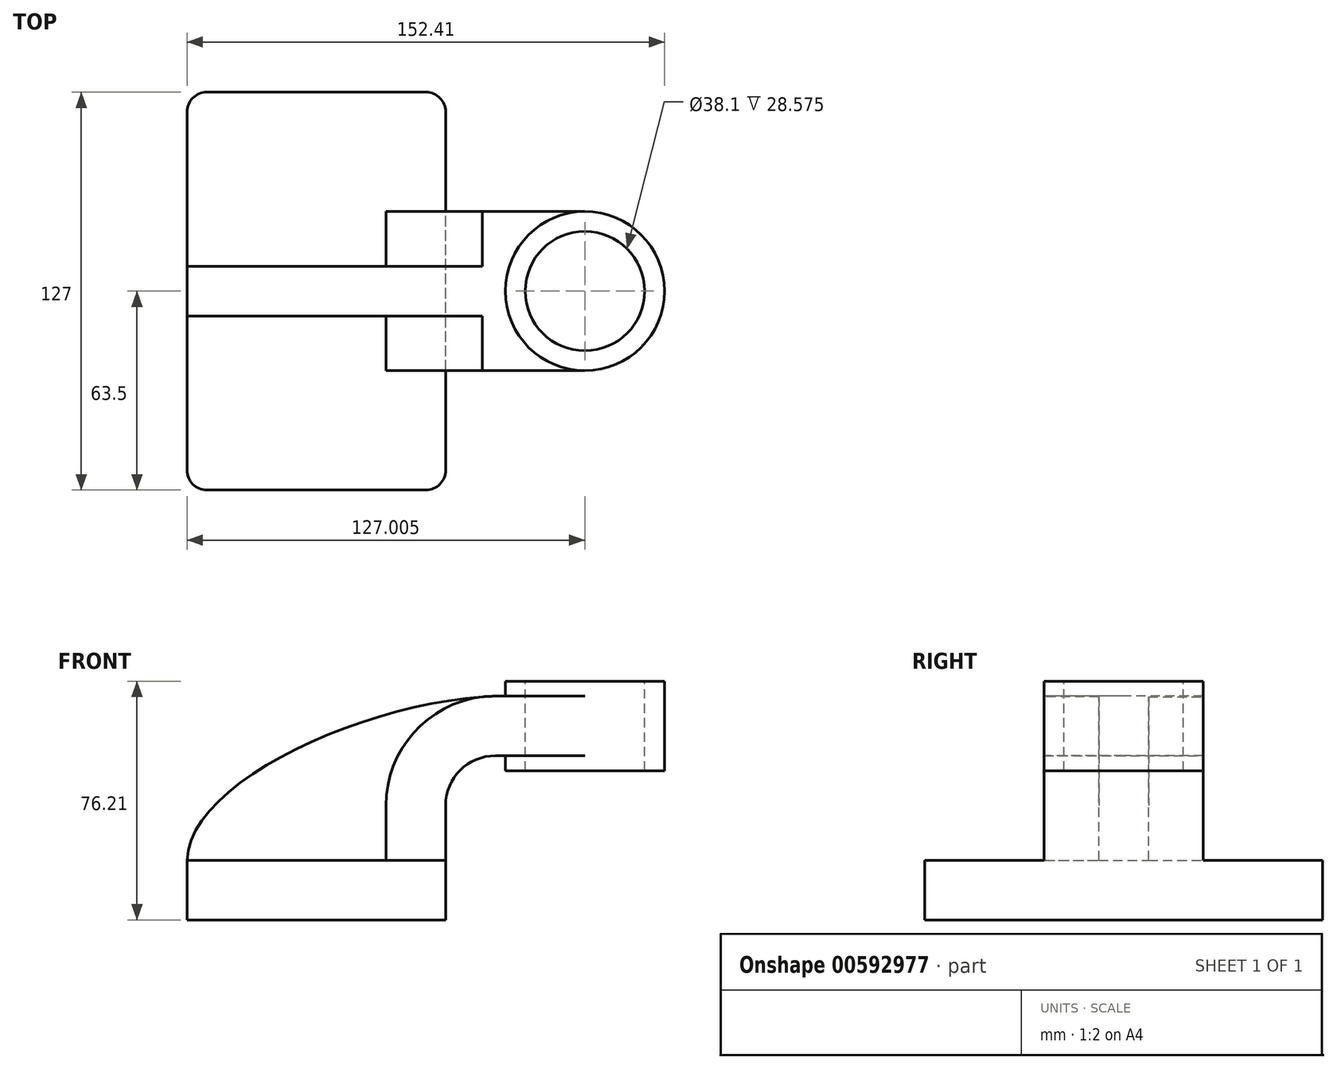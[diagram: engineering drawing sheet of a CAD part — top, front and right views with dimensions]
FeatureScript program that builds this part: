
annotation { "Feature Type Name" : "Feature", "Feature Type Description" : "" }
export const myFeature = defineFeature(function(context is Context, id is Id, definition is map)
    precondition{}
    {
        {
            var Q0;
            Q0=qCreatedBy(makeId("Front.planeOp"),FACE);
            var sketch = newSketch(context, id + "F0", { "sketchPlane" : qUnion([Q0])});
            skLineSegment(sketch, "E0.bottom", {"start": v(-41.27, 9.53) * mm, "end": v(41.28, 9.53) * mm});
            skLineSegment(sketch, "E0.top", {"start": v(-41.28, -9.52) * mm, "end": v(41.27, -9.52) * mm});
            skLineSegment(sketch, "E0.left", {"start": v(-41.28, 9.53) * mm, "end": v(-41.28, -9.52) * mm});
            skLineSegment(sketch, "E0.right", {"start": v(41.28, 9.53) * mm, "end": v(41.27, -9.52) * mm});
            skPoint(sketch, "E0.middle", {"position": v(0, 0) * mm});
            skLineSegment(sketch, "E1.bottom", {"start": v(111.12, 66.68) * mm, "end": v(60.32, 66.68) * mm});
            skLineSegment(sketch, "E1.top", {"start": v(111.12, 38.1) * mm, "end": v(60.33, 38.1) * mm});
            skLineSegment(sketch, "E1.left", {"start": v(111.12, 66.67) * mm, "end": v(111.12, 38.1) * mm});
            skLineSegment(sketch, "E1.right", {"start": v(60.32, 66.67) * mm, "end": v(60.32, 38.1) * mm});
            skPoint(sketch, "E1.middle", {"position": v(85.72, 52.39) * mm});
            skLineSegment(sketch, "E2", {"start": v(41.28, 9.53) * mm, "end": v(41.28, 27) * mm});
            skArc(sketch, "E3", {"start": v(41.28, 27) * mm, "mid": v(45.92, 38.23) * mm, "end": v(57.15, 42.88) * mm});
            skLineSegment(sketch, "E4", {"start": v(57.15, 42.88) * mm, "end": v(105.55, 42.88) * mm});
            skLineSegment(sketch, "E5.0", {"start": v(57.15, 61.93) * mm, "end": v(105.55, 61.93) * mm});
            skArc(sketch, "E5.1", {"start": v(22.23, 27) * mm, "mid": v(32.45, 51.7) * mm, "end": v(57.15, 61.93) * mm});
            skLineSegment(sketch, "E5.2", {"start": v(22.23, 9.52) * mm, "end": v(22.23, 27) * mm});
            skLineSegment(sketch, "E6", {"start": v(85.72, 38.1) * mm, "end": v(85.72, 66.68) * mm});
            skFitSpline(sketch, "E7", {"points": [v(-41.28, 9.53) * mm, v(60.32, 61.93) * mm], "startDerivative": vector(1.14, 77.5) * mm, "endDerivative": vector(120.84, -0.42) * mm});
            skSolve(sketch);
        }
        {
            var Q0;
            Q0=makeQuery(id+"F0.imprint","IMPRINT",FACE,{"disambiguationData":[TD([[makeQuery(id+"F0.imprint","IMPRINT",EDGE,{"derivedFrom":sQuery(id+"F0.wireOp",EDGE,"E0.top")}),1.0]])]});
            extrude(context, id + "F1", {"entities" : qUnion([Q0]), "endBound" : BoundingType.SYMMETRIC, "depth" : 127 * mm, "offsetDistance" : 25.4 * mm});
        }
        {
            var Q0;
            {var subQ1=sQuery(id+"F0.wireOp",EDGE,"E2");Q0=makeQuery(id+"F0.imprint","IMPRINT",FACE,{"disambiguationData":[TD([[makeQuery(id+"F0.imprint","IMPRINT",EDGE,{"derivedFrom":subQ1}),1.0]])]});}
            var Q1;
            {var subQ1=sQuery(id+"F0.wireOp",EDGE,"E1.right");var subQ3=sQuery(id+"F0.wireOp",EDGE,"E4");var subQ4=makeQuery(id+"F0.imprint","INTERSECT",VERTEX,{"derivedFrom":[subQ1,subQ3]});Q1=makeQuery(id+"F0.imprint","IMPRINT",FACE,{"disambiguationData":[TD([[makeQuery(id+"F0.imprint","IMPRINT",EDGE,{"disambiguationData":[TD([[subQ4,-1.0]])],"derivedFrom":subQ3}),1.0]])]});}
            extrude(context, id + "F2", {"entities" : qUnion([Q0, Q1]), "operationType" : NewBodyOperationType.ADD, "endBound" : BoundingType.SYMMETRIC, "depth" : 50.8 * mm, "offsetDistance" : 25.4 * mm});
        }
        {
            var Q0;
            {var subQ3=sQuery(id+"F0.wireOp",EDGE,"E5.2");Q0=makeQuery(id+"F0.imprint","IMPRINT",FACE,{"disambiguationData":[TD([[makeQuery(id+"F0.imprint","IMPRINT",EDGE,{"derivedFrom":subQ3}),1.0]])]});}
            extrude(context, id + "F3", {"entities" : qUnion([Q0]), "operationType" : NewBodyOperationType.ADD, "endBound" : BoundingType.SYMMETRIC, "depth" : 15.88 * mm, "offsetDistance" : 25.4 * mm});
        }
        {
            var Q0;
            {var subQ4=sQuery(id+"F0.wireOp",EDGE,"E1.left");Q0=makeQuery(id+"F0.imprint","IMPRINT",FACE,{"disambiguationData":[TD([[makeQuery(id+"F0.imprint","IMPRINT",EDGE,{"derivedFrom":subQ4}),-1.0]])]});}
            var Q1;
            Q1=sQuery(id+"F0.wireOp",EDGE,"E6");
            revolve(context, id + "F4", {"operationType" : NewBodyOperationType.ADD, "entities" : qUnion([Q0]), "axis" : qUnion([Q1]), "revolveType" : RevolveType.FULL});
        }
        {
            var Q0;
            Q0=makeQuery(id+"F1.opExtrude","CAP_EDGE",EDGE,{"disambiguationData":[OSD([sQuery(id+"F0.wireOp",EDGE,"E0.right")])],"isStart":false});
            var Q1;
            Q1=makeQuery(id+"F1.opExtrude","CAP_EDGE",EDGE,{"disambiguationData":[OSD([sQuery(id+"F0.wireOp",EDGE,"E0.left")])],"isStart":false});
            var Q2;
            Q2=makeQuery(id+"F1.opExtrude","CAP_EDGE",EDGE,{"disambiguationData":[OSD([sQuery(id+"F0.wireOp",EDGE,"E0.right")])],"isStart":true});
            var Q3;
            Q3=makeQuery(id+"F1.opExtrude","CAP_EDGE",EDGE,{"disambiguationData":[OSD([sQuery(id+"F0.wireOp",EDGE,"E0.left")])],"isStart":true});
            fillet(context, id + "F5", {"entities" : qUnion([Q0, Q1, Q2, Q3]), "radius" : 6.35 * mm, "tangentPropagation" : true, "allowEdgeOverflow" : false});
        }
        {
            var Q0;
            Q0=makeQuery(id+"F4.opRevolve","SWEPT_FACE",FACE,{"disambiguationData":[OSD([sQuery(id+"F0.wireOp",EDGE,"E1.bottom")])]});
            var sketch = newSketch(context, id + "F6", { "sketchPlane" : qUnion([Q0])});
            skCircle(sketch, "E8", {"center": v(85.72, 0) * mm, "radius": 19.05 * mm});
            skSolve(sketch);
        }
        {
            var Q0;
            Q0 = qSketchRegion(id + "F6", true);
            extrude(context, id + "F7", {"entities" : qUnion([Q0]), "operationType" : NewBodyOperationType.REMOVE, "endBound" : BoundingType.UP_TO_NEXT, "oppositeDirection" : true, "depth" : 25.4 * mm, "offsetDistance" : 25.4 * mm});
        }
    });
